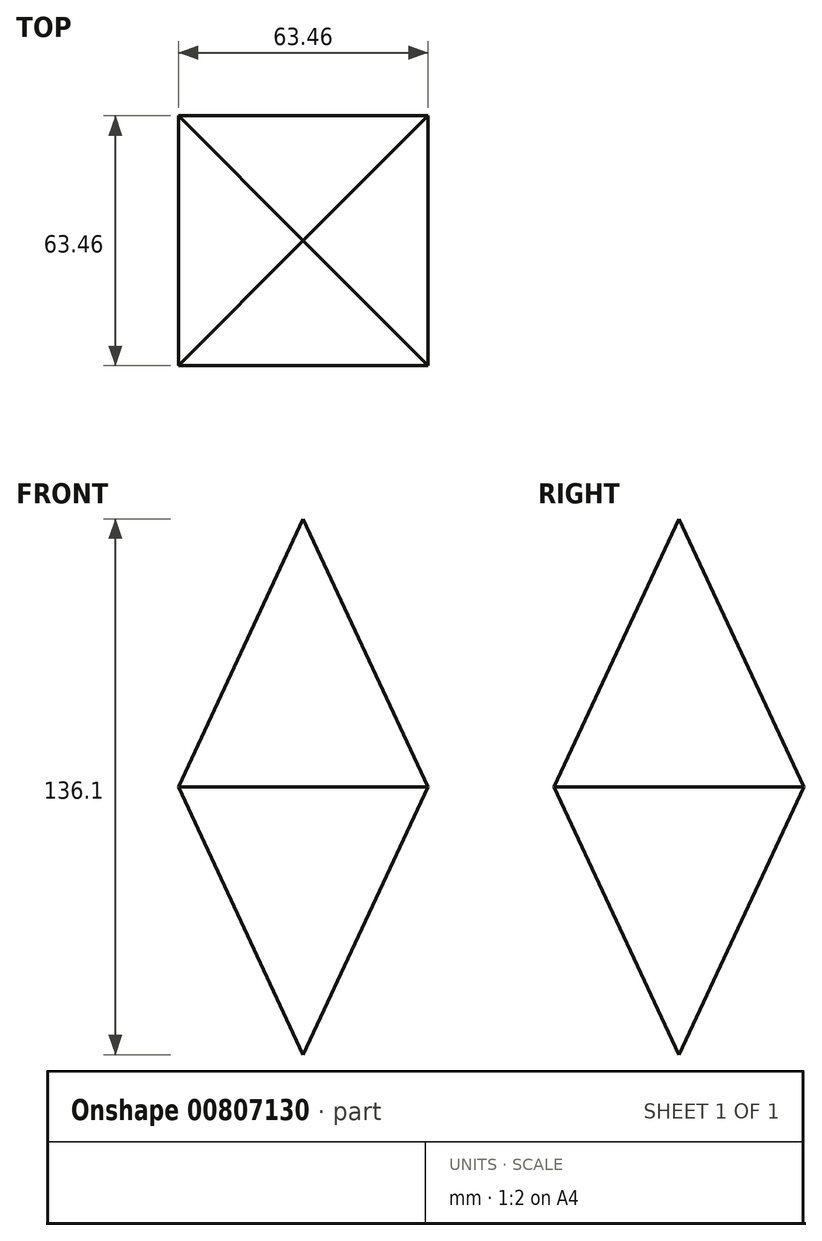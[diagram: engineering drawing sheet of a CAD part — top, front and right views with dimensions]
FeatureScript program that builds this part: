
annotation { "Feature Type Name" : "Feature", "Feature Type Description" : "" }
export const myFeature = defineFeature(function(context is Context, id is Id, definition is map)
    precondition{}
    {
        {
            var Q0;
            Q0=qCreatedBy(makeId("Top.planeOp"),FACE);
            var sketch = newSketch(context, id + "F0", { "sketchPlane" : qUnion([Q0])});
            skLineSegment(sketch, "E0.bottom", {"start": v(31.73, 31.73) * mm, "end": v(-31.73, 31.73) * mm});
            skLineSegment(sketch, "E0.top", {"start": v(31.73, -31.73) * mm, "end": v(-31.73, -31.73) * mm});
            skLineSegment(sketch, "E0.left", {"start": v(31.73, 31.73) * mm, "end": v(31.73, -31.73) * mm});
            skLineSegment(sketch, "E0.right", {"start": v(-31.73, 31.73) * mm, "end": v(-31.73, -31.73) * mm});
            skPoint(sketch, "E0.middle", {"position": v(0, 0) * mm});
            skSolve(sketch);
        }
        {
            var Q0;
            Q0=makeQuery(id+"F0.imprint","IMPRINT",FACE,{"disambiguationData":[TD([[makeQuery(id+"F0.imprint","IMPRINT",EDGE,{"derivedFrom":sQuery(id+"F0.wireOp",EDGE,"E0.bottom")}),1.0]])]});
            extrude(context, id + "F1", {"entities" : qUnion([Q0]), "depth" : 88.4 * mm, "offsetDistance" : 25.4 * mm, "hasDraft" : true, "draftAngle" : 25 * degree, "draftPullDirection" : true, "hasSecondDirection" : true, "secondDirectionOppositeDirection" : true, "secondDirectionDepth" : 87.63 * mm, "hasSecondDirectionDraft" : true, "secondDirectionDraftAngle" : 25 * degree, "secondDirectionDraftPullDirection" : true});
        }
    });
